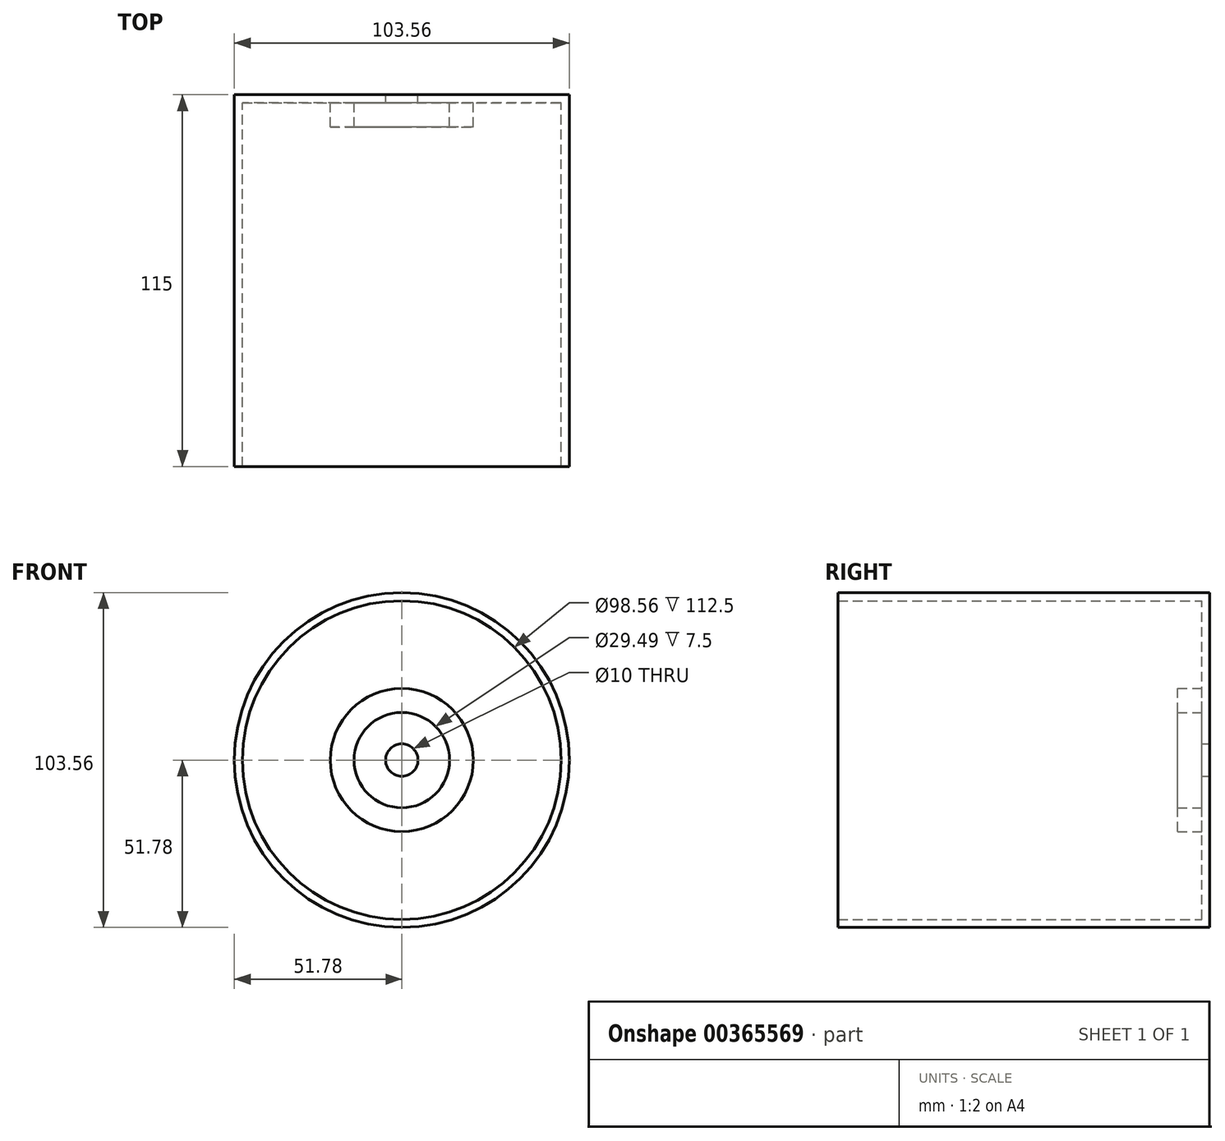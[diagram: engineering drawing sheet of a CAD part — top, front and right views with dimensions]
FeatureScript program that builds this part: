
annotation { "Feature Type Name" : "Feature", "Feature Type Description" : "" }
export const myFeature = defineFeature(function(context is Context, id is Id, definition is map)
    precondition{}
    {
        {
            var Q0;
            Q0=qCreatedBy(makeId("Front.planeOp"),FACE);
            var sketch = newSketch(context, id + "F0", { "sketchPlane" : qUnion([Q0])});
            skCircle(sketch, "E0", {"center": v(0, 0) * mm, "radius": 51.78 * mm});
            skSolve(sketch);
        }
        {
            var Q0;
            Q0 = qSketchRegion(id + "F0", true);
            extrude(context, id + "F1", {"entities" : qUnion([Q0]), "depth" : 100 * mm});
        }
        {
            var Q0;
            Q0=makeQuery(id+"F1.opExtrude","CAP_FACE",FACE,{"disambiguationData":[OSD([sQuery(id+"F0.wireOp",EDGE,"E0")])],"isStart":false});
            shell(context, id + "F2", {"entities" : qUnion([Q0]), "thickness" : 2.5 * mm});
        }
        {
            var Q0;
            Q0=qCreatedBy(makeId("Front.planeOp"),FACE);
            var sketch = newSketch(context, id + "F3", { "sketchPlane" : qUnion([Q0])});
            skCircle(sketch, "E1", {"center": v(0, 0) * mm, "radius": 22.12 * mm});
            skCircle(sketch, "E2", {"center": v(0, 0) * mm, "radius": 14.75 * mm});
            skSolve(sketch);
        }
        {
            var Q0;
            Q0 = qSketchRegion(id + "F3", true);
            extrude(context, id + "F4", {"entities" : qUnion([Q0]), "operationType" : NewBodyOperationType.ADD, "depth" : 10 * mm});
        }
        {
            var Q0;
            Q0=qCreatedBy(makeId("Front.planeOp"),FACE);
            var sketch = newSketch(context, id + "F5", { "sketchPlane" : qUnion([Q0])});
            skPoint(sketch, "E3", {"position": v(0, 0) * mm});
            skSolve(sketch);
        }
        {
            var Q0;
            Q0=sQuery(id+"F5.wireOp",VERTEX,"E3");
            var Q1;
            Q1=makeQuery(id+"F1.opExtrude","SWEPT_BODY",BODY,{"disambiguationData":[OSD([sQuery(id+"F0.wireOp",EDGE,"E0")])]});
            hole(context, id + "F6", {"style" : HoleStyle.C_BORE, "endStyle" : HoleEndStyle.THROUGH, "oppositeDirection" : true, "holeDiameter" : 10 * mm, "cBoreDiameter" : 10 * mm, "cBoreDepth" : 5 * mm, "isTappedThrough" : true, "tappedDepth" : 12 * mm, "tapClearance" : 3, "locations" : qUnion([Q0]), "scope" : qUnion([Q1])});
        }
        {
            var Q0;
            Q0=makeQuery(id+"F1.opExtrude","CAP_FACE",FACE,{"disambiguationData":[OSD([sQuery(id+"F0.wireOp",EDGE,"E0")])],"isStart":false});
            extrude(context, id + "F7", {"entities" : qUnion([Q0]), "operationType" : NewBodyOperationType.ADD, "depth" : 5 * mm});
        }
        {
            var Q0;
            Q0=makeQuery(id+"F7.opExtrude","CAP_FACE",FACE,{"disambiguationData":[OSD([sQuery(id+"F0.wireOp",EDGE,"E0")])],"isStart":false});
            extrude(context, id + "F8", {"entities" : qUnion([Q0]), "operationType" : NewBodyOperationType.ADD, "depth" : 10 * mm});
        }
    });
